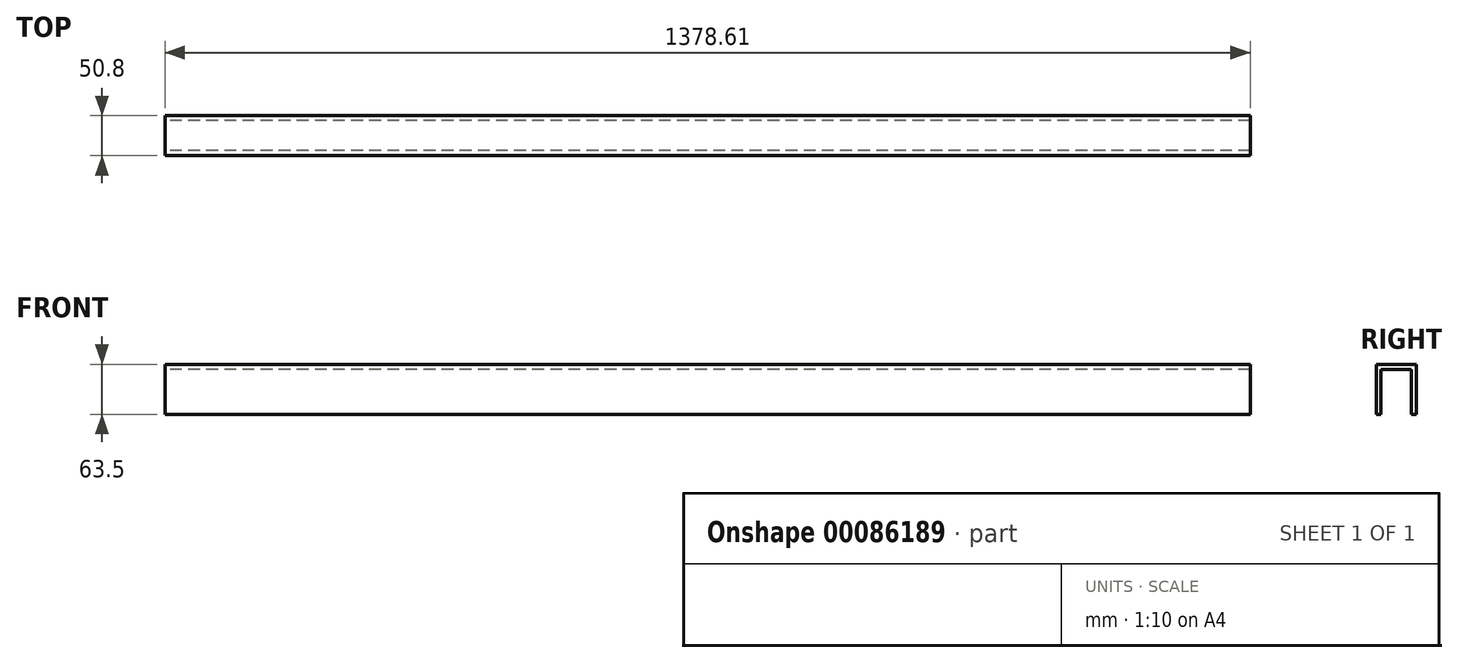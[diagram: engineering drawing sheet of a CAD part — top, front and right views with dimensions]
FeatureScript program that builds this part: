
annotation { "Feature Type Name" : "Feature", "Feature Type Description" : "" }
export const myFeature = defineFeature(function(context is Context, id is Id, definition is map)
    precondition{}
    {
        {
            var Q0;
            Q0=qCreatedBy(makeId("Front.planeOp"),FACE);
            var sketch = newSketch(context, id + "F0", { "sketchPlane" : qUnion([Q0])});
            skLineSegment(sketch, "E0.bottom", {"start": v(0, 0) * mm, "end": v(-1378.61, 0) * mm});
            skLineSegment(sketch, "E0.top", {"start": v(0, 63.5) * mm, "end": v(-1378.61, 63.5) * mm});
            skLineSegment(sketch, "E0.left", {"start": v(0, 0) * mm, "end": v(0, 63.5) * mm});
            skLineSegment(sketch, "E0.right", {"start": v(-1378.61, 0) * mm, "end": v(-1378.61, 63.5) * mm});
            skSolve(sketch);
        }
        {
            var Q0;
            Q0=makeQuery(id+"F0.imprint","IMPRINT",FACE,{"disambiguationData":[TD([[makeQuery(id+"F0.imprint","IMPRINT",EDGE,{"derivedFrom":sQuery(id+"F0.wireOp",EDGE,"E0.bottom")}),-1.0]])]});
            extrude(context, id + "F1", {"entities" : qUnion([Q0]), "depth" : 50.8 * mm});
        }
        {
            var Q0;
            Q0=makeQuery(id+"F1.opExtrude","SWEPT_FACE",FACE,{"disambiguationData":[OSD([sQuery(id+"F0.wireOp",EDGE,"E0.right")])]});
            var sketch = newSketch(context, id + "F2", { "sketchPlane" : qUnion([Q0])});
            skLineSegment(sketch, "E1.0", {"start": v(0, 0) * mm, "end": v(0, 63.5) * mm});
            skLineSegment(sketch, "E1.1", {"start": v(50.8, 63.5) * mm, "end": v(0, 63.5) * mm});
            skLineSegment(sketch, "E1.2", {"start": v(50.8, 0) * mm, "end": v(50.8, 63.5) * mm});
            skLineSegment(sketch, "E2.0", {"start": v(44.45, 0) * mm, "end": v(44.45, 57.15) * mm});
            skLineSegment(sketch, "E2.1", {"start": v(44.45, 57.15) * mm, "end": v(6.35, 57.15) * mm});
            skLineSegment(sketch, "E2.2", {"start": v(6.35, 0) * mm, "end": v(6.35, 57.15) * mm});
            skLineSegment(sketch, "E3", {"start": v(6.35, 0) * mm, "end": v(44.45, 0) * mm});
            skSolve(sketch);
        }
        {
            var Q0;
            Q0=makeQuery(id+"F2.imprint","IMPRINT",FACE,{"disambiguationData":[TD([[makeQuery(id+"F2.imprint","IMPRINT",EDGE,{"derivedFrom":sQuery(id+"F2.wireOp",EDGE,"E2.0")}),1.0]])]});
            extrude(context, id + "F3", {"entities" : qUnion([Q0]), "operationType" : NewBodyOperationType.REMOVE, "endBound" : BoundingType.THROUGH_ALL, "oppositeDirection" : true, "depth" : 25.4 * mm});
        }
    });
